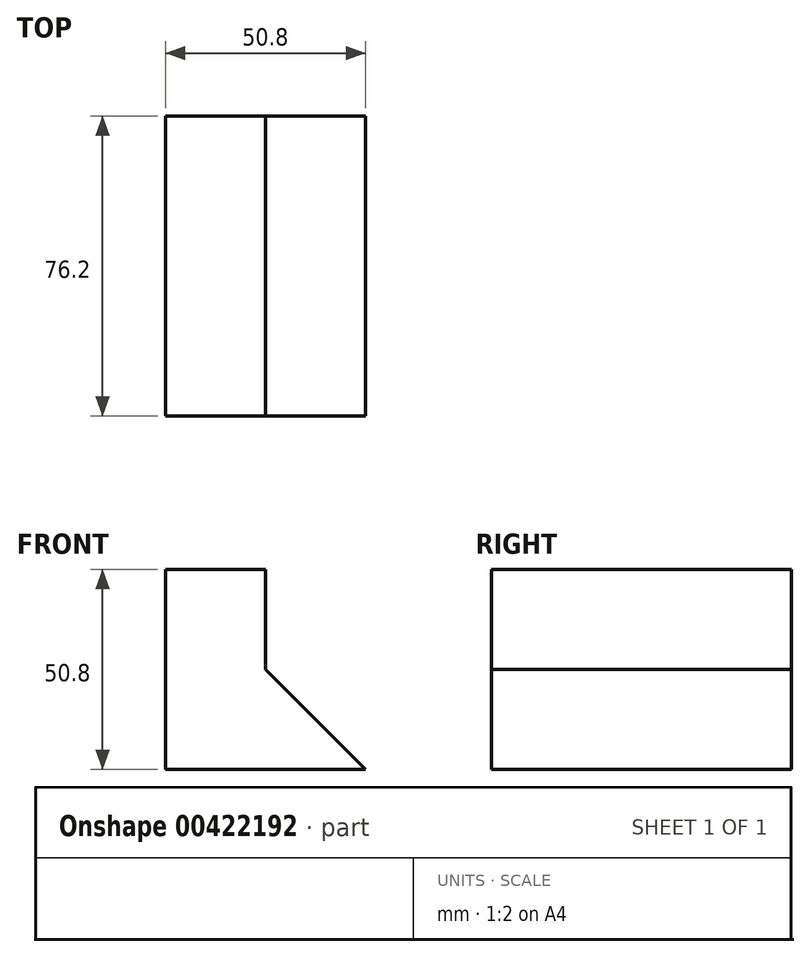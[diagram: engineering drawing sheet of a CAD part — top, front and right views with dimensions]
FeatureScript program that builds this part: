
annotation { "Feature Type Name" : "Feature", "Feature Type Description" : "" }
export const myFeature = defineFeature(function(context is Context, id is Id, definition is map)
    precondition{}
    {
        {
            var Q0;
            Q0=qCreatedBy(makeId("Front.planeOp"),FACE);
            var sketch = newSketch(context, id + "F0", { "sketchPlane" : qUnion([Q0])});
            skLineSegment(sketch, "E0", {"start": v(0, 0) * mm, "end": v(-50.8, 0) * mm});
            skLineSegment(sketch, "E1", {"start": v(-50.8, 0) * mm, "end": v(-50.8, 50.8) * mm});
            skLineSegment(sketch, "E2", {"start": v(-50.8, 50.8) * mm, "end": v(-25.4, 50.8) * mm});
            skLineSegment(sketch, "E3", {"start": v(-25.4, 50.8) * mm, "end": v(-25.4, 25.4) * mm});
            skLineSegment(sketch, "E4", {"start": v(-25.4, 25.4) * mm, "end": v(0, 0) * mm});
            skSolve(sketch);
        }
        {
            var Q0;
            Q0 = qSketchRegion(id + "F0", true);
            extrude(context, id + "F1", {"entities" : qUnion([Q0]), "depth" : 76.2 * mm});
        }
    });
